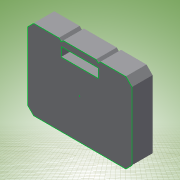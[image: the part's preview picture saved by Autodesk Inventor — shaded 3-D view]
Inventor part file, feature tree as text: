
AUTODESK INVENTOR PART (.ipt)
format: ipt  version: 2017 (Build 210142000, 142)  size: 174,080 bytes
history: native  units: in
note: dims shown in document units (in); Inventor stores cm internally (conversion verified against a paired STEP export)
features: extrude x3, sketch x3, chamfer x2, projected_geometry x2
ambient origin geometry x8: Origin, YZ Plane, XZ Plane, XY Plane, X Axis, Y Axis, Z Axis, Center Point
bodies: Solid1 (feature_tree)
feature tree (10):
  extrude  "Extrusion1"  Depth=13.0in
  chamfer  "Chamfer1"  Distance=3.375in
  extrude  "Extrusion2"  Depth=1.0in
  extrude  "Extrusion3"  Depth=1.0in TaperAngle=45.0deg
  chamfer  "Chamfer2"  Distance=1.1875in
  sketch  "Sketch1"  dims[d0=17.0in d1=13.0in d2=3.375in d3=0.0in]
  sketch  "Sketch2"  dims[d5=5.5in d6=5.5in d7=10.5in d11=1.0in]
  projected_geometry  "Projected Loop1"
  sketch  "Sketch3"  dims[d12=45.0deg d13=1.0in d14=0.125in d15=45.0deg d17=1.1875in d18=0.0in d19=1.1875in d20=0.0in d21=0.125in d22=0.125in d23=45.0deg]
  projected_geometry  "Projected Loop2"
